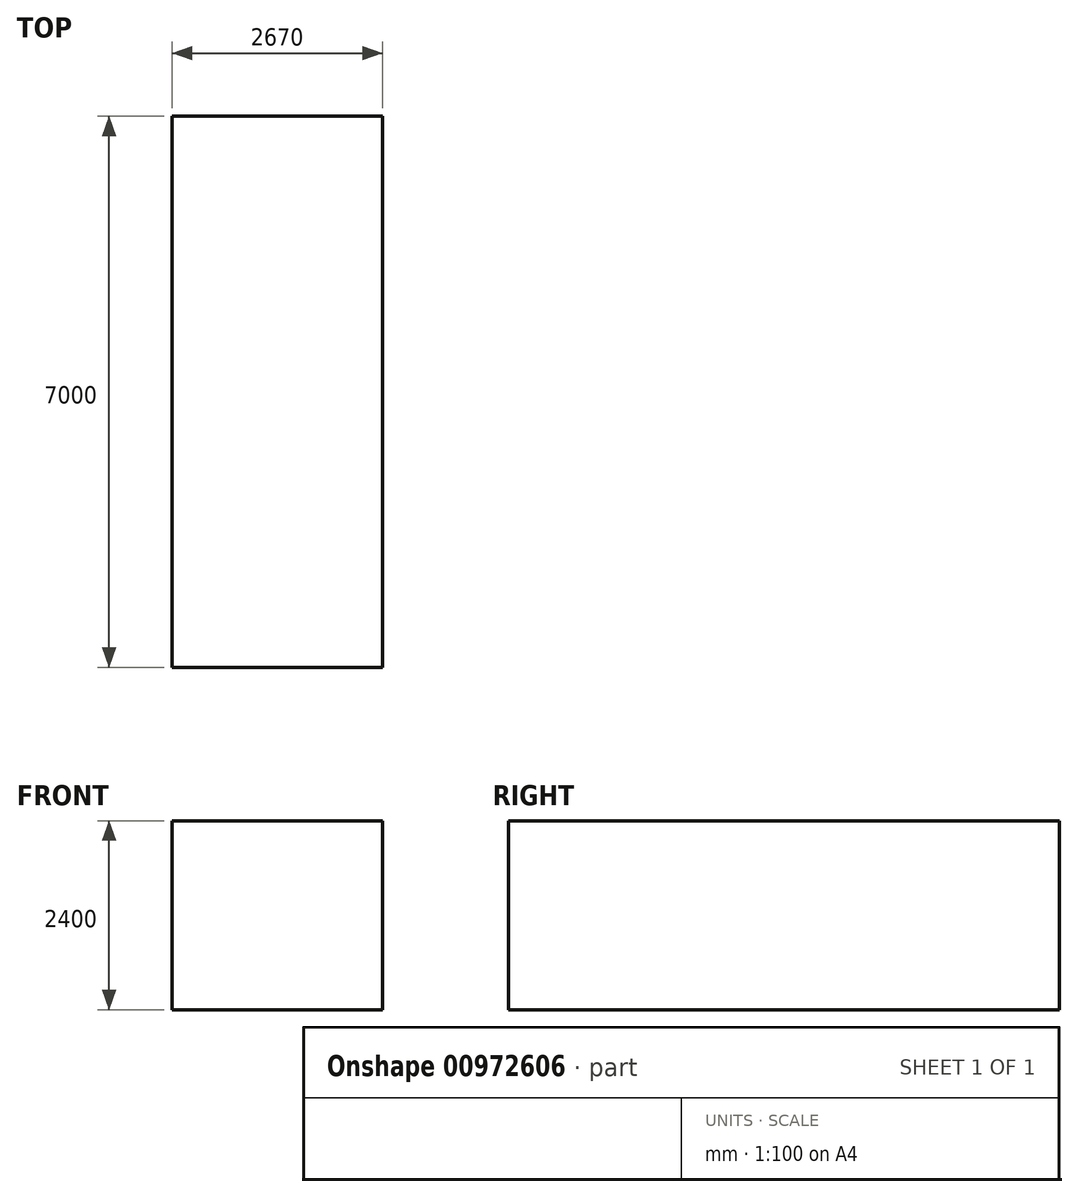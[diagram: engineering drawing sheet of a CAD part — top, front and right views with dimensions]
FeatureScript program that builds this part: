
annotation { "Feature Type Name" : "Feature", "Feature Type Description" : "" }
export const myFeature = defineFeature(function(context is Context, id is Id, definition is map)
    precondition{}
    {
        {
            var Q0;
            Q0=qCreatedBy(makeId("Top.planeOp"),FACE);
            var sketch = newSketch(context, id + "F0", { "sketchPlane" : qUnion([Q0])});
            skLineSegment(sketch, "E0.bottom", {"start": v(0, 0) * mm, "end": v(2670, 0) * mm});
            skLineSegment(sketch, "E0.top", {"start": v(0, 7000) * mm, "end": v(2670, 7000) * mm});
            skLineSegment(sketch, "E0.left", {"start": v(0, 0) * mm, "end": v(0, 7000) * mm});
            skLineSegment(sketch, "E0.right", {"start": v(2670, 0) * mm, "end": v(2670, 7000) * mm});
            skSolve(sketch);
        }
        {
            var Q0;
            Q0=makeQuery(id+"F0.imprint","IMPRINT",FACE,{"disambiguationData":[TD([[makeQuery(id+"F0.imprint","IMPRINT",EDGE,{"derivedFrom":sQuery(id+"F0.wireOp",EDGE,"E0.bottom")}),1.0]])]});
            extrude(context, id + "F1", {"entities" : qUnion([Q0]), "depth" : 2400 * mm, "offsetDistance" : 25 * mm});
        }
    });
